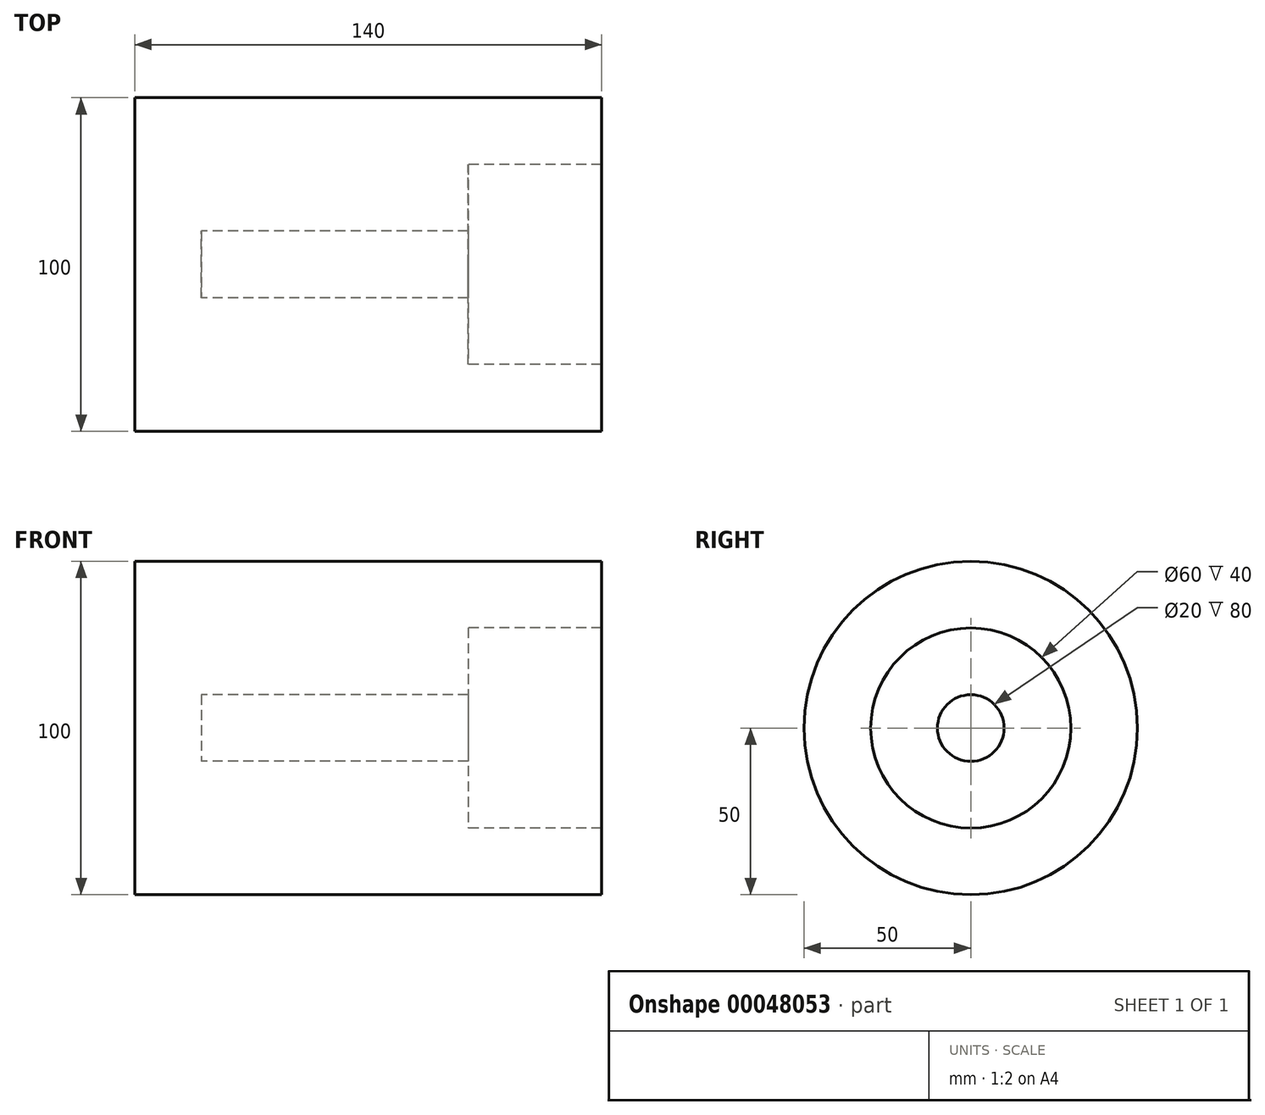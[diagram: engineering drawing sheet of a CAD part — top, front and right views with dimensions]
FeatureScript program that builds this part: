
annotation { "Feature Type Name" : "Feature", "Feature Type Description" : "" }
export const myFeature = defineFeature(function(context is Context, id is Id, definition is map)
    precondition{}
    {
        {
            var Q0;
            Q0=qCreatedBy(makeId("Front.planeOp"),FACE);
            var sketch = newSketch(context, id + "F0", { "sketchPlane" : qUnion([Q0])});
            skLineSegment(sketch, "E0.bottom", {"start": v(0, 0) * mm, "end": v(140, 0) * mm});
            skLineSegment(sketch, "E0.top", {"start": v(0, 100) * mm, "end": v(140, 100) * mm});
            skLineSegment(sketch, "E0.left", {"start": v(0, 0) * mm, "end": v(0, 100) * mm});
            skLineSegment(sketch, "E0.right", {"start": v(140, 0) * mm, "end": v(140, 100) * mm});
            skLineSegment(sketch, "E1", {"start": v(0, 50) * mm, "end": v(140, 50) * mm});
            skLineSegment(sketch, "E2.bottom", {"start": v(140, 20) * mm, "end": v(100, 20) * mm});
            skLineSegment(sketch, "E2.top", {"start": v(140, 80) * mm, "end": v(100, 80) * mm});
            skLineSegment(sketch, "E2.left", {"start": v(140, 20) * mm, "end": v(140, 80) * mm});
            skLineSegment(sketch, "E2.right", {"start": v(100, 20) * mm, "end": v(100, 80) * mm});
            skLineSegment(sketch, "E3.bottom", {"start": v(100, 40) * mm, "end": v(20, 40) * mm});
            skLineSegment(sketch, "E3.top", {"start": v(100, 60) * mm, "end": v(20, 60) * mm});
            skLineSegment(sketch, "E3.left", {"start": v(100, 40) * mm, "end": v(100, 60) * mm});
            skLineSegment(sketch, "E3.right", {"start": v(20, 40) * mm, "end": v(20, 60) * mm});
            skPoint(sketch, "E4", {"position": v(100, 50) * mm});
            skSolve(sketch);
        }
        {
            var Q0;
            {var subQ4=sQuery(id+"F0.wireOp",EDGE,"E0.bottom");Q0=makeQuery(id+"F0.imprint","IMPRINT",FACE,{"disambiguationData":[TD([[makeQuery(id+"F0.imprint","IMPRINT",EDGE,{"derivedFrom":subQ4}),1.0]])]});}
            var Q1;
            Q1=sQuery(id+"F0.wireOp",EDGE,"E1");
            revolve(context, id + "F1", {"entities" : qUnion([Q0]), "axis" : qUnion([Q1]), "revolveType" : RevolveType.FULL});
        }
    });
